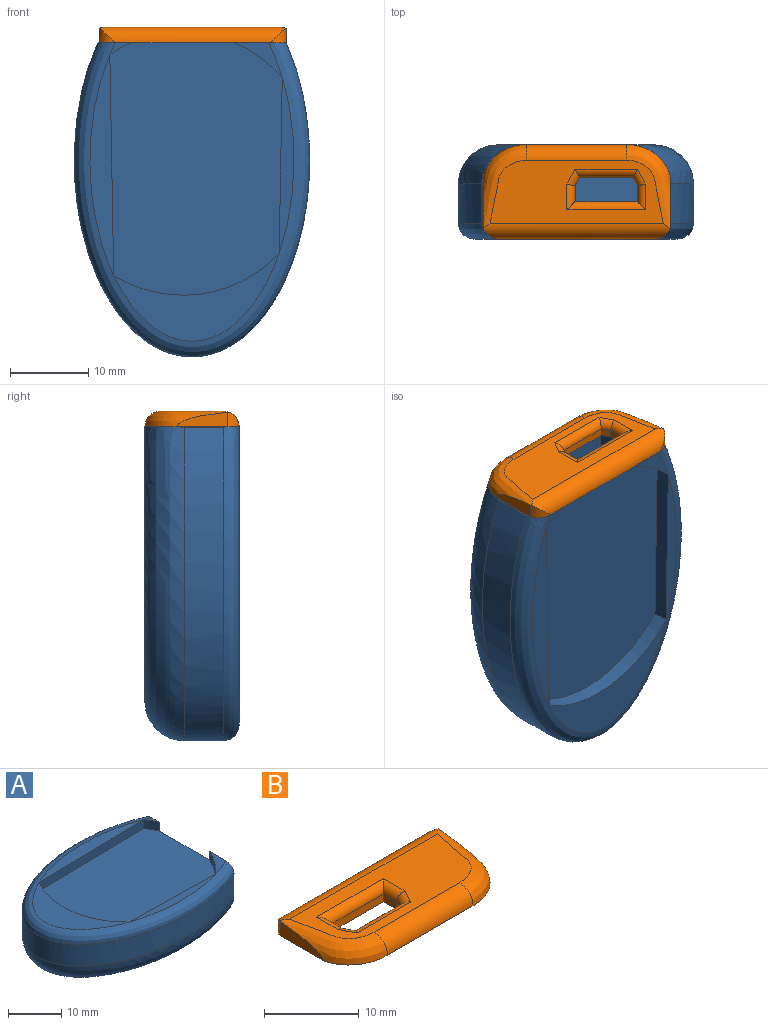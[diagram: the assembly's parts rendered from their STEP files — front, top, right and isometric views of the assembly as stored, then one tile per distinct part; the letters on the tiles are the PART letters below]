
ASSEMBLY  parts=2 mates=1
PART A: 28 faces, bbox 44.4x30.3x12.2 mm
  f0: plane 28.16x3.04mm, normal (0,0,1), area 53.3mm2, adj f11,f23
  f1: plane 2.73x1.49mm, normal (0,0,1), area 1.4mm2, adj f4,f11,f22
  f2: plane 6.05x4.42mm, normal (0,0,1), area 7.7mm2, adj f4,f11,f26
  f3: plane 22.43x1.9mm, normal (0,0,1), area 25.6mm2, adj f11,f25
  f4: plane 24.07x12.24mm, normal (1,0,0), area 115.6mm2, adj f1,f2,f5,f7,f9,f10,f11,f12
  f5: cylinder r=0.13mm len=6.44mm, axis (0,0,-1), area 0.9mm2, adj f4,f6,f10,f11
  f6: extruded ~39.92x29.96mm, area 472.3mm2, adj f5,f7,f10,f11
  f7: cylinder r=0.13mm len=6.44mm, axis (0,0,-1), area 0.9mm2, adj f4,f6,f10,f11
  f8: plane 21.09x11.18mm, normal (0,0,1), area 88.2mm2, adj f11,f24
  f9: plane 35.01x20.01mm, normal (0,0,-1), area 575.6mm2, adj f4,f10
  f10: bspline ~44.16x30.02mm, area 699.4mm2, adj f4,f5,f6,f7,f9
  f11: bspline ~42.05x30.02mm, area 290.6mm2, adj f0,f1,f2,f3,f4,f5,f6,f7
  f12: plane 30x7.25mm, normal (0,1,0), area 217.5mm2, adj f4,f13,f15,f16
  f13: plane 30x8.85mm, normal (0,0,1), area 265.5mm2, adj f4,f12,f14,f16
  f14: plane 30x7.25mm, normal (0,-1,0), area 217.5mm2, adj f4,f13,f15,f16
  f15: plane 30x8.85mm, normal (0,0,-1), area 265.5mm2, adj f4,f12,f14,f16
  f16: plane 8.85x7.25mm, normal (1,0,0), area 64.2mm2, adj f12,f13,f14,f15
  f17: plane 30x7.25mm, normal (0,1,0), area 217.5mm2, adj f4,f18,f20,f21
  f18: plane 30x9.25mm, normal (0,0,1), area 277.5mm2, adj f4,f17,f19,f21
  f19: plane 30x7.25mm, normal (0,-1,0), area 217.5mm2, adj f4,f18,f20,f21
  f20: plane 30x9.25mm, normal (0,0,-1), area 277.5mm2, adj f4,f17,f19,f21
  f21: plane 9.25x7.25mm, normal (1,0,0), area 67.1mm2, adj f17,f18,f19,f20
  f22: cylinder r=16.75mm len=2.73mm, axis (0,0,1), area 6.2mm2, adj f1,f4,f23,f27
  f23: plane 28.15x2mm, normal (0.02,-1,0), area 56.3mm2, adj f0,f22,f24,f27
  f24: cylinder r=16.75mm len=21.08mm, axis (0,0,1), area 46.1mm2, adj f8,f23,f25,f27
  f25: plane 22.42x2mm, normal (0.02,1,0), area 44.8mm2, adj f3,f24,f26,f27
  f26: cylinder r=16.75mm len=6.04mm, axis (0,0,1), area 15.1mm2, adj f2,f4,f25,f27
  f27: plane 32.15x21.97mm, normal (0,0,1), area 651mm2, adj f4,f22,f23,f24,f25,f26
PART B: 22 faces, bbox 28x15x2 mm
  f0: extruded ~2.12x1.88mm, area 3mm2, adj f1,f11,f12,f14
  f1: plane 6.44x1.85mm, normal (-1,0,0), area 8.6mm2, adj f0,f11,f12
  f2: plane 6.44x1.85mm, normal (1,0,0), area 8.6mm2, adj f9,f11,f15
  f3: plane 8x1mm, normal (0,-1,0), area 8mm2, adj f4,f8,f11,f19
  f4: plane 1.99x1mm, normal (-1,0,0), area 2mm2, adj f3,f5,f11,f17
  f5: plane 1.11x1mm, normal (-0.88,0.48,0), area 1.3mm2, adj f4,f6,f11,f16
  f6: plane 6.8x1mm, normal (0,1,0), area 6.8mm2, adj f5,f7,f11,f18
  f7: plane 1.11x1mm, normal (0.88,0.48,0), area 1.3mm2, adj f6,f8,f11,f20
  f8: plane 1.99x1mm, normal (1,0,0), area 2mm2, adj f3,f7,f11,f21
  f9: extruded ~2.12x1.88mm, area 3mm2, adj f2,f11,f14,f15
  f10: plane 22.08x8mm, normal (0,0,1), area 111.7mm2, adj f12,f13,f14,f15,f16,f17,f18,f19
  f11: plane 23.83x12mm, normal (0,0,-1), area 249.1mm2, adj f0,f1,f2,f3,f4,f5,f6,f7
  f12: bspline ~15.04x9.74mm, area 30.3mm2, adj f0,f1,f10,f11,f13,f14
  f13: cylinder r=2mm len=12.76mm, axis (-1,0,0), area 40.1mm2, adj f10,f11,f12,f15
  f14: cylinder r=2mm len=23.73mm, axis (1,0,0), area 68.9mm2, adj f0,f9,f10,f11,f12,f15
  f15: bspline ~15.02x9.75mm, area 30.3mm2, adj f2,f9,f10,f11,f13,f14
  f16: cylinder r=1mm len=2.33mm, axis (0.48,0.88,0), area 2.6mm2, adj f5,f10,f17,f18
  f17: cylinder r=1mm len=3.24mm, axis (0,1,0), area 4.1mm2, adj f4,f10,f16,f19
  f18: cylinder r=1mm len=7.99mm, axis (1,0,0), area 11.6mm2, adj f6,f10,f16,f20
  f19: cylinder r=1mm len=10mm, axis (-1,0,0), area 14.1mm2, adj f3,f10,f17,f21
  f20: cylinder r=1mm len=2.33mm, axis (0.48,-0.88,0), area 2.6mm2, adj f7,f10,f18,f21
  f21: cylinder r=1mm len=3.24mm, axis (0,-1,0), area 4.1mm2, adj f8,f10,f19,f20
PLACE A rot(axis=(0.58,-0.58,0.58),120deg) t=(17.4,-21.82,45.7)mm
PLACE B rot(axis=(0,0,-1),180deg) t=(-22.57,-1.51,45.7)mm
MATE planar A.f4 <-> B.f11  axis (0,0,1) through (8.65,-25.51,45.7)mm
